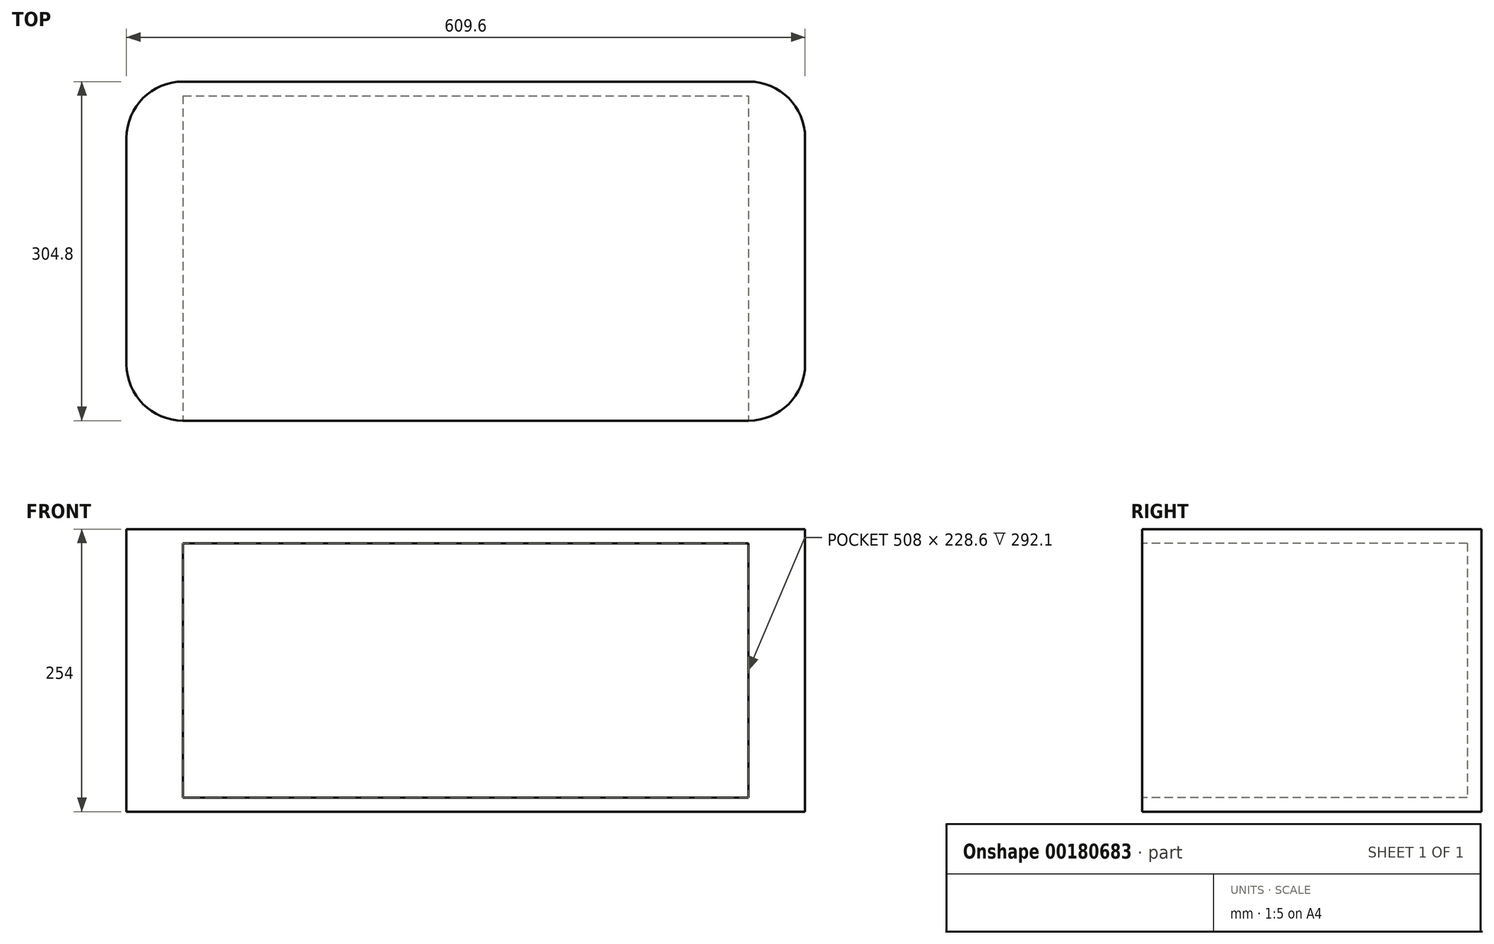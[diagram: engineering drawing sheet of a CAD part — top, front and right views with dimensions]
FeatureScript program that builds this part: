
annotation { "Feature Type Name" : "Feature", "Feature Type Description" : "" }
export const myFeature = defineFeature(function(context is Context, id is Id, definition is map)
    precondition{}
    {
        {
            var Q0;
            Q0=qCreatedBy(makeId("Top.planeOp"),FACE);
            var sketch = newSketch(context, id + "F0", { "sketchPlane" : qUnion([Q0])});
            skLineSegment(sketch, "E0.bottom", {"start": v(-254, -152.4) * mm, "end": v(254, -152.4) * mm});
            skLineSegment(sketch, "E0.top", {"start": v(-254, 152.4) * mm, "end": v(254, 152.4) * mm});
            skLineSegment(sketch, "E0.left", {"start": v(-304.8, -101.6) * mm, "end": v(-304.8, 101.6) * mm});
            skLineSegment(sketch, "E0.right", {"start": v(304.8, -101.6) * mm, "end": v(304.8, 101.6) * mm});
            skPoint(sketch, "E0.middle", {"position": v(0, 0) * mm});
            skPoint(sketch, "E1.visualSharp", {"position": v(-304.8, -152.4) * mm});
            skArc(sketch, "E1.filletArc", {"start": v(-304.8, -101.6) * mm, "mid": v(-289.92, -137.52) * mm, "end": v(-254, -152.4) * mm});
            skPoint(sketch, "E2.visualSharp", {"position": v(304.8, -152.4) * mm});
            skArc(sketch, "E2.filletArc", {"start": v(254, -152.4) * mm, "mid": v(289.92, -137.52) * mm, "end": v(304.8, -101.6) * mm});
            skPoint(sketch, "E3.visualSharp", {"position": v(304.8, 152.4) * mm});
            skArc(sketch, "E3.filletArc", {"start": v(304.8, 101.6) * mm, "mid": v(289.92, 137.52) * mm, "end": v(254, 152.4) * mm});
            skPoint(sketch, "E4.visualSharp", {"position": v(-304.8, 152.4) * mm});
            skArc(sketch, "E4.filletArc", {"start": v(-254, 152.4) * mm, "mid": v(-289.92, 137.52) * mm, "end": v(-304.8, 101.6) * mm});
            skSolve(sketch);
        }
        {
            var Q0;
            Q0=makeQuery(id+"F0.imprint","IMPRINT",FACE,{"disambiguationData":[TD([[makeQuery(id+"F0.imprint","IMPRINT",EDGE,{"derivedFrom":sQuery(id+"F0.wireOp",EDGE,"E0.bottom")}),1.0]])]});
            extrude(context, id + "F1", {"entities" : qUnion([Q0]), "depth" : 254 * mm});
        }
        {
            var Q0;
            Q0=makeQuery(id+"F1.opExtrude","SWEPT_FACE",FACE,{"disambiguationData":[OSD([sQuery(id+"F0.wireOp",EDGE,"E0.bottom")])]});
            var sketch = newSketch(context, id + "F2", { "sketchPlane" : qUnion([Q0])});
            skLineSegment(sketch, "E5", {"start": v(-254, 241.3) * mm, "end": v(254, 241.3) * mm});
            skLineSegment(sketch, "E6", {"start": v(-254, 12.7) * mm, "end": v(254, 12.7) * mm});
            skSolve(sketch);
        }
        {
            var Q0;
            {var subQ0=sQuery(id+"F2.wireOp",EDGE,"E5");Q0=makeQuery(id+"F2.imprint","IMPRINT",FACE,{"disambiguationData":[TD([[makeQuery(id+"F2.imprint","IMPRINT",EDGE,{"derivedFrom":subQ0}),-1.0]])]});}
            extrude(context, id + "F3", {"entities" : qUnion([Q0]), "operationType" : NewBodyOperationType.REMOVE, "oppositeDirection" : true, "depth" : 292.1 * mm});
        }
    });
